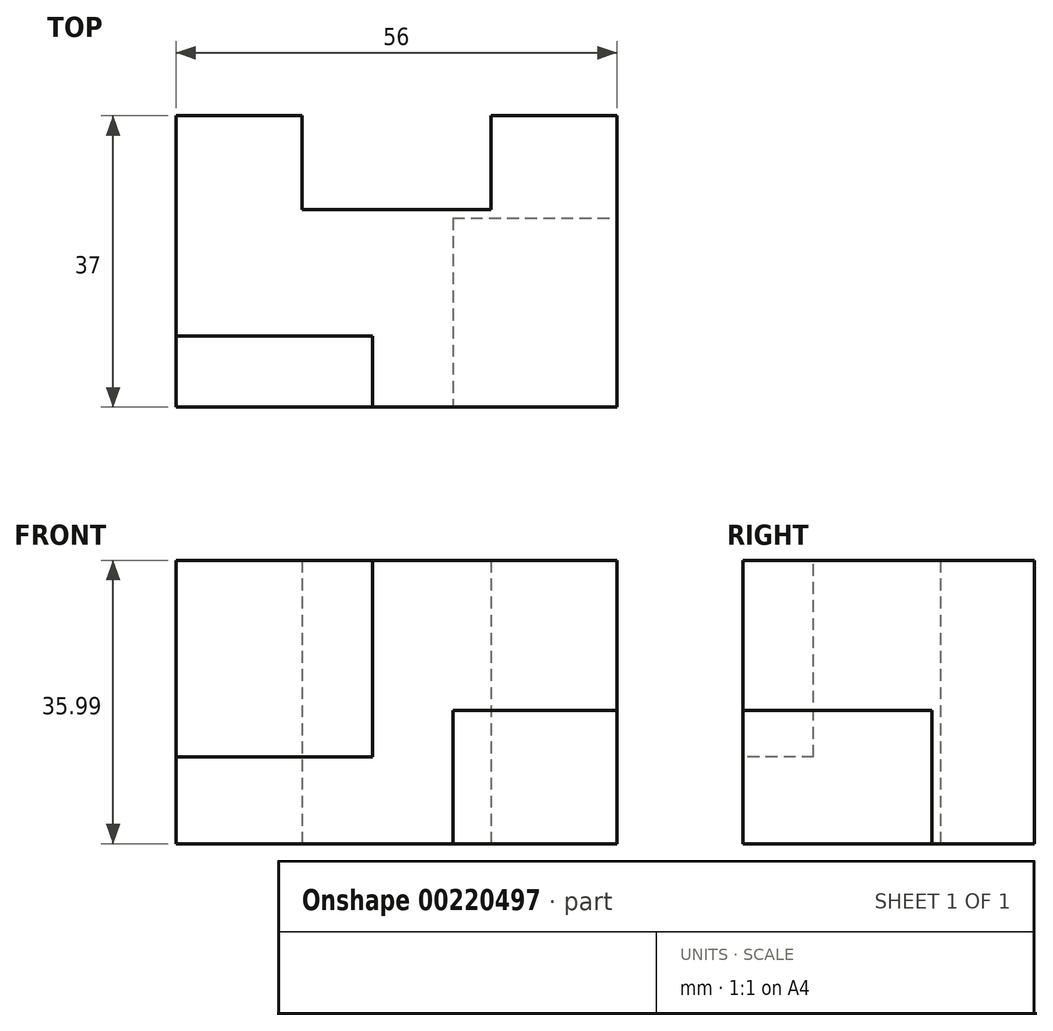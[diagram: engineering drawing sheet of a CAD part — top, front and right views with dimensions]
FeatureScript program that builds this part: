
annotation { "Feature Type Name" : "Feature", "Feature Type Description" : "" }
export const myFeature = defineFeature(function(context is Context, id is Id, definition is map)
    precondition{}
    {
        {
            var Q0;
            Q0=qCreatedBy(makeId("Top.planeOp"),FACE);
            var sketch = newSketch(context, id + "F0", { "sketchPlane" : qUnion([Q0])});
            skLineSegment(sketch, "E0.bottom", {"start": v(28, 18.5) * mm, "end": v(12, 18.5) * mm});
            skLineSegment(sketch, "E0.top", {"start": v(28, -18.5) * mm, "end": v(-28, -18.5) * mm});
            skLineSegment(sketch, "E0.left", {"start": v(28, 18.5) * mm, "end": v(28, -18.5) * mm});
            skLineSegment(sketch, "E0.right", {"start": v(-28, 18.5) * mm, "end": v(-28, -18.5) * mm});
            skPoint(sketch, "E0.middle", {"position": v(0, 0) * mm});
            skLineSegment(sketch, "E1.0", {"start": v(-12, 18.5) * mm, "end": v(-12, 6.57) * mm});
            skLineSegment(sketch, "E2.0", {"start": v(12, 18.5) * mm, "end": v(12, 6.57) * mm});
            skLineSegment(sketch, "E3.0", {"start": v(12, 6.57) * mm, "end": v(-12, 6.57) * mm});
            skLineSegment(sketch, "E4.trimOffspring", {"start": v(-12, 18.5) * mm, "end": v(-28, 18.5) * mm});
            skSolve(sketch);
        }
        {
            var Q0;
            Q0=makeQuery(id+"F0.imprint","IMPRINT",FACE,{"disambiguationData":[TD([[makeQuery(id+"F0.imprint","IMPRINT",EDGE,{"derivedFrom":sQuery(id+"F0.wireOp",EDGE,"E0.bottom")}),1.0]])]});
            extrude(context, id + "F1", {"entities" : qUnion([Q0]), "depth" : 36 * mm});
        }
        {
            var Q0;
            Q0=makeQuery(id+"F1.opExtrude","SWEPT_FACE",FACE,{"disambiguationData":[OSD([sQuery(id+"F0.wireOp",EDGE,"E0.left")])]});
            var sketch = newSketch(context, id + "F2", { "sketchPlane" : qUnion([Q0])});
            skLineSegment(sketch, "E5.bottom", {"start": v(-18.5, 0) * mm, "end": v(5.5, 0) * mm});
            skLineSegment(sketch, "E5.top", {"start": v(-18.5, 16.94) * mm, "end": v(5.5, 16.94) * mm});
            skLineSegment(sketch, "E5.left", {"start": v(-18.5, 0) * mm, "end": v(-18.5, 16.94) * mm});
            skLineSegment(sketch, "E5.right", {"start": v(5.5, 0) * mm, "end": v(5.5, 16.94) * mm});
            skSolve(sketch);
        }
        {
            var Q0;
            Q0=makeQuery(id+"F2.imprint","IMPRINT",FACE,{"disambiguationData":[TD([[makeQuery(id+"F2.imprint","IMPRINT",EDGE,{"derivedFrom":sQuery(id+"F2.wireOp",EDGE,"E5.bottom")}),-1.0]])]});
            extrude(context, id + "F3", {"entities" : qUnion([Q0]), "operationType" : NewBodyOperationType.REMOVE, "oppositeDirection" : true, "depth" : 20.85 * mm});
        }
        {
            var Q0;
            Q0=makeQuery(id+"F1.opExtrude","CAP_FACE",FACE,{"disambiguationData":[OSD([sQuery(id+"F0.wireOp",EDGE,"E0.bottom"),sQuery(id+"F0.wireOp",EDGE,"E0.top"),sQuery(id+"F0.wireOp",EDGE,"E0.left"),sQuery(id+"F0.wireOp",EDGE,"E0.right"),sQuery(id+"F0.wireOp",EDGE,"E1.0"),sQuery(id+"F0.wireOp",EDGE,"E2.0"),sQuery(id+"F0.wireOp",EDGE,"E3.0"),sQuery(id+"F0.wireOp",EDGE,"E4.trimOffspring")])],"isStart":false});
            var sketch = newSketch(context, id + "F4", { "sketchPlane" : qUnion([Q0])});
            skLineSegment(sketch, "E6.bottom", {"start": v(-28, -18.5) * mm, "end": v(-3.04, -18.5) * mm});
            skLineSegment(sketch, "E6.top", {"start": v(-28, -9.51) * mm, "end": v(-3.04, -9.51) * mm});
            skLineSegment(sketch, "E6.left", {"start": v(-28, -18.5) * mm, "end": v(-28, -9.51) * mm});
            skLineSegment(sketch, "E6.right", {"start": v(-3.04, -18.5) * mm, "end": v(-3.04, -9.51) * mm});
            skSolve(sketch);
        }
        {
            var Q0;
            Q0=makeQuery(id+"F4.imprint","IMPRINT",FACE,{"disambiguationData":[TD([[makeQuery(id+"F4.imprint","IMPRINT",EDGE,{"derivedFrom":sQuery(id+"F4.wireOp",EDGE,"E6.bottom")}),-1.0]])]});
            extrude(context, id + "F5", {"entities" : qUnion([Q0]), "operationType" : NewBodyOperationType.REMOVE, "oppositeDirection" : true, "depth" : 24.94 * mm});
        }
    });
